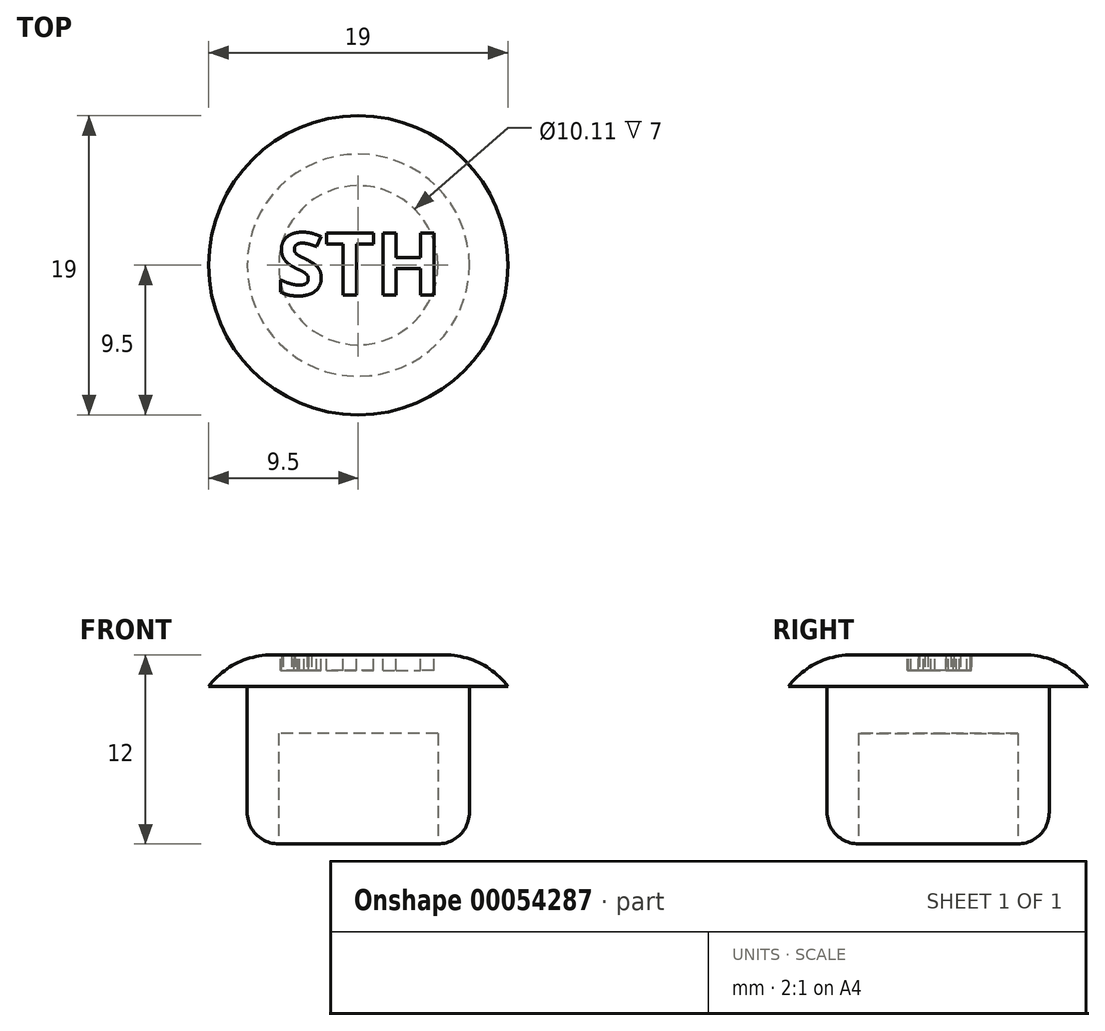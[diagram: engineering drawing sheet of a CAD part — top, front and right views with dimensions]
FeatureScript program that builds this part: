
annotation { "Feature Type Name" : "Feature", "Feature Type Description" : "" }
export const myFeature = defineFeature(function(context is Context, id is Id, definition is map)
    precondition{}
    {
        {
            var Q0;
            Q0=qCreatedBy(makeId("Top.planeOp"),FACE);
            var sketch = newSketch(context, id + "F0", { "sketchPlane" : qUnion([Q0])});
            skCircle(sketch, "E0", {"center": v(0, 0) * mm, "radius": 7.05 * mm});
            skSolve(sketch);
        }
        {
            var Q0;
            Q0 = qSketchRegion(id + "F0", true);
            extrude(context, id + "F1", {"entities" : qUnion([Q0]), "depth" : 10 * mm});
        }
        {
            var Q0;
            Q0=makeQuery(id+"F1.opExtrude","CAP_FACE",FACE,{"disambiguationData":[OSD([sQuery(id+"F0.wireOp",EDGE,"E0")])],"isStart":false});
            var sketch = newSketch(context, id + "F2", { "sketchPlane" : qUnion([Q0])});
            skCircle(sketch, "E1", {"center": v(0, 0) * mm, "radius": 9.5 * mm});
            skSolve(sketch);
        }
        {
            var Q0;
            Q0=makeQuery(id+"F2.imprint","IMPRINT",FACE,{"disambiguationData":[TD([[makeQuery(id+"F2.imprint","IMPRINT",EDGE,{"derivedFrom":makeQuery(id+"F1.opExtrude","CAP_EDGE",EDGE,{"disambiguationData":[OSD([sQuery(id+"F0.wireOp",EDGE,"E0")])],"isStart":false})}),1.0]])]});
            var Q1;
            Q1=makeQuery(id+"F2.imprint","IMPRINT",FACE,{"disambiguationData":[TD([[makeQuery(id+"F2.imprint","IMPRINT",EDGE,{"derivedFrom":sQuery(id+"F2.wireOp",EDGE,"E1")}),1.0]])]});
            extrude(context, id + "F3", {"entities" : qUnion([Q0, Q1]), "operationType" : NewBodyOperationType.ADD, "depth" : 2 * mm});
        }
        {
            var Q0;
            Q0=makeQuery(id+"F3.opExtrude","CAP_EDGE",EDGE,{"disambiguationData":[OSD([sQuery(id+"F2.wireOp",EDGE,"E1")])],"isStart":false});
            fillet(context, id + "F4", {"entities" : qUnion([Q0]), "radius" : 5 * mm, "tangentPropagation" : true, "allowEdgeOverflow" : false});
        }
        {
            var Q0;
            Q0=makeQuery(id+"F1.opExtrude","CAP_EDGE",EDGE,{"disambiguationData":[OSD([sQuery(id+"F0.wireOp",EDGE,"E0")])],"isStart":true});
            fillet(context, id + "F5", {"entities" : qUnion([Q0]), "radius" : 2 * mm, "tangentPropagation" : true, "allowEdgeOverflow" : false});
        }
        {
            var Q0;
            Q0=makeQuery(id+"F3.opExtrude","CAP_FACE",FACE,{"disambiguationData":[OSD([sQuery(id+"F2.wireOp",EDGE,"E1")])],"isStart":false});
            var sketch = newSketch(context, id + "F6", { "sketchPlane" : qUnion([Q0])});
            skText(sketch, "E2", { "text": "STH", "fontName": "OpenSans-Bold.ttf"});
            const initialGuessF6  = {"E2": [-0.00518, -0.0019, 1, 0, 0.00398]};
            skSetInitialGuess(sketch, initialGuessF6);
            skSolve(sketch);
        }
        {
            var Q0;
            Q0 = qSketchRegion(id + "F6", true);
            var Q1;
            Q1=makeQuery(id+"F6.imprint","IMPRINT",FACE,{"disambiguationData":[TD([[makeQuery(id+"F6.imprint","IMPRINT",EDGE,{"derivedFrom":sQuery(id+"F6.wireOp",EDGE,"E2.sketch_text.stroke-28")}),-1.0]])]});
            extrude(context, id + "F7", {"entities" : qUnion([Q0, Q1]), "operationType" : NewBodyOperationType.REMOVE, "oppositeDirection" : true, "depth" : 1 * mm});
        }
        {
            var Q0;
            Q0=makeQuery(id+"F1.opExtrude","CAP_FACE",FACE,{"disambiguationData":[OSD([sQuery(id+"F0.wireOp",EDGE,"E0")])],"isStart":true});
            extrude(context, id + "F8", {"entities" : qUnion([Q0]), "operationType" : NewBodyOperationType.REMOVE, "oppositeDirection" : true, "depth" : 7 * mm});
        }
    });
